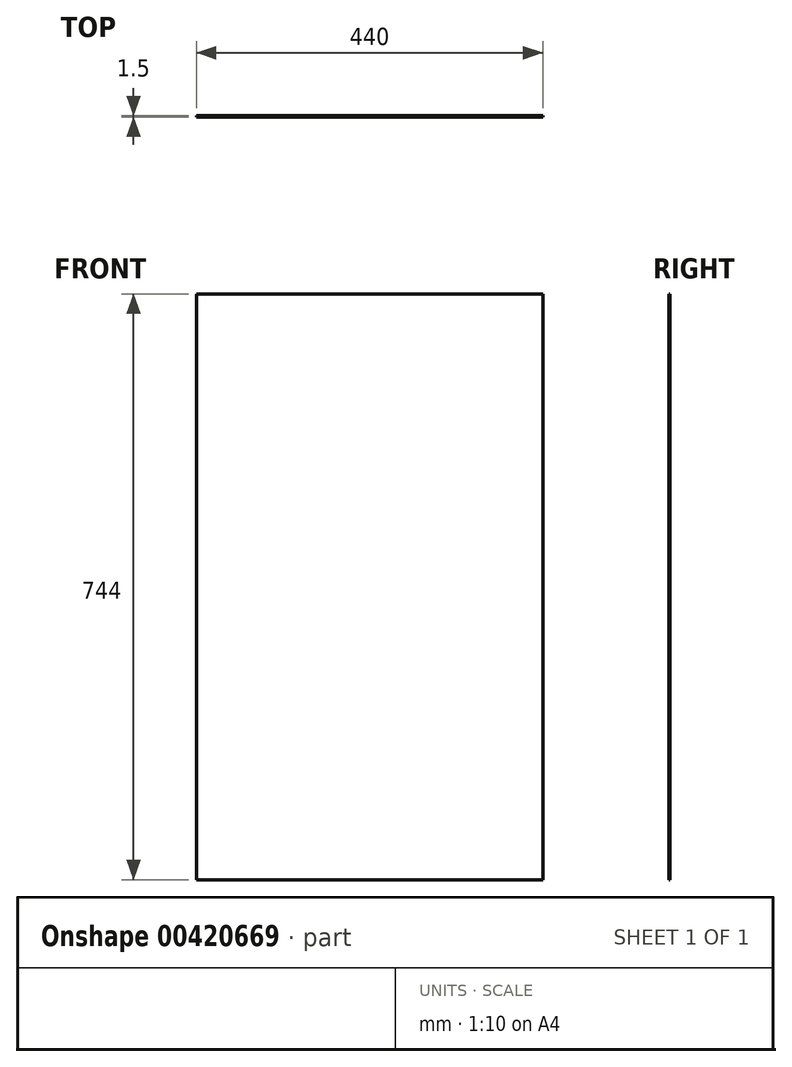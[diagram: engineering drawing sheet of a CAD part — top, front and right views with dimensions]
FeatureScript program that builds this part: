
annotation { "Feature Type Name" : "Feature", "Feature Type Description" : "" }
export const myFeature = defineFeature(function(context is Context, id is Id, definition is map)
    precondition{}
    {
        {
            var Q0;
            Q0=qCreatedBy(makeId("Front.planeOp"),FACE);
            var sketch = newSketch(context, id + "F0", { "sketchPlane" : qUnion([Q0])});
            skLineSegment(sketch, "E0.bottom", {"start": v(220, -372) * mm, "end": v(-220, -372) * mm});
            skLineSegment(sketch, "E0.top", {"start": v(220, 372) * mm, "end": v(-220, 372) * mm});
            skLineSegment(sketch, "E0.left", {"start": v(220, -372) * mm, "end": v(220, 372) * mm});
            skLineSegment(sketch, "E0.right", {"start": v(-220, -372) * mm, "end": v(-220, 372) * mm});
            skPoint(sketch, "E0.middle", {"position": v(0, 0) * mm});
            skSolve(sketch);
        }
        {
            var Q0;
            Q0=qSketchRegion(id+"F0",true);
            extrude(context, id + "F1", {"entities" : qUnion([Q0]), "depth" : 1.5 * mm});
        }
    });
